# Revit family: RN 81035 Optipress-Aquaplus-Übergang
name_source: partatom
category: Rohrformteile
units: mm (PartAtom-declared; Revit-internal decimal feet)

## family parameters
Arbeitsebenenbasiert = Nein
Beim Laden mit Abzugskörper schneiden = Nein
Bemaßung runder Anschluss = Durchmesser verwenden
Gemeinsam genutzt = Nein
Immer vertikal = Ja
Teiletyp = Verbindung

## types (20) — shared parameters
1.010.00.2 Blattnummer der Richtlinie = 29
1.010.00.3 Ausgabedatum (Monat) der Richtlinie = 201308
1.010.00.4 Herstellername = R. Nussbaum AG
1.010.00.5 Revisionsdatum der Datei = 20190521
1.010.00.6 Webadresse des Herstellers = http://www.nussbaum.ch
1.100.00.4 Produktbezeichnung = Versorgung
1.110.00.2 Index = 4
1.110.00.4 Produktbezeichnung = Optipress
1.960/3L.00.8 Link (URL) = https://www.nussbaum.ch
29.700.00.4 Produktname = Optipress-Aquaplus-Übergang, mit Aussengewinde
29.700.00.5 Produktkennung = 2
29.700.00.6 Querschnittsform = 1
29.700.00.7 Nennweitensystem = DN
29.700.00.8 Nenndrucksystem = PN
29.710.02.4 Nenndruck = 16
29.710.02.5 max. zul. Überdruck [hPa] = 1600
29.710.02.7 max. zul. Dauer-Betriebsdruck [hPa] = 1600
29.710.02.9 max. zul. Dauer-Betriebstemperatur [°C] = 95
Connector Visibility = Nein
EnclosingSpace Visibility = Nein

## per-type parameters (varying)
- 81035.18, Optipress-Aquaplus-Übergang, mit Aussengewinde, DN=10, L=35, R=3/8: 1.800.00.3 TGA-Nummer=01900400000000000000000000000000000000000000000024000000000000000020; 1.810.00.3 Hersteller-Bestellnummer=81035.18; 1.810.00.4 DATANORM-Nummer=81035.18; 1.810.00.6 GTIN-Nummer=7612945021618; 29.710.02.10 Formstück-Gewicht [kg]=0.03; 29.710.02.3 Benennung=Optipress-Aquaplus-Übergang, mit Aussengewinde, DN=10, L=35, R=3/8; CONNECTOR0_DIAMETER_dX_0r=10 mm  [stored 0.0328084 ft]; CONNECTOR0_dX_01=18 mm; CONNECTOR0_ref_dX=18 mm; CONNECTOR1_DIAMETER_dX_0r=12 mm  [stored 0.0393701 ft]; CONNECTOR1_dX_00=25 mm  [stored 0.082021 ft]; CONNECTOR1_dX_01=35 mm; CONNECTOR1_ref_dX=25 mm  [stored 0.082021 ft]; R. Nussbaum AG 81035.18 de Visibility=Ja; R. Nussbaum AG 81035.19 de Visibility=Nein; R. Nussbaum AG 81035.20 de Visibility=Nein; R. Nussbaum AG 81035.21 de Visibility=Nein; R. Nussbaum AG 81035.22 de Visibility=Nein; R. Nussbaum AG 81035.23 de Visibility=Nein; R. Nussbaum AG 81035.24 de Visibility=Nein; R. Nussbaum AG 81035.25 de Visibility=Nein; R. Nussbaum AG 81035.27 de Visibility=Nein; R. Nussbaum AG 81035.28 de Visibility=Nein; R. Nussbaum AG 81035.29 de Visibility=Nein; R. Nussbaum AG 81035.30 de Visibility=Nein; R. Nussbaum AG 81035.31 de Visibility=Nein; R. Nussbaum AG 81035.32 de Visibility=Nein; R. Nussbaum AG 81035.33 de Visibility=Nein; R. Nussbaum AG 81035.34 de Visibility=Nein; R. Nussbaum AG 81035.36 de Visibility=Nein; R. Nussbaum AG 81035.37 de Visibility=Nein; R. Nussbaum AG 81035.38 de Visibility=Nein; R. Nussbaum AG 81035.39 de Visibility=Nein
- 81035.19, Optipress-Aquaplus-Übergang, mit Aussengewinde, DN=10x15, L=37, R=½: 1.800.00.3 TGA-Nummer=01900400000000000000000000000000000000000000000024000000000000000021; 1.810.00.3 Hersteller-Bestellnummer=81035.19; 1.810.00.4 DATANORM-Nummer=81035.19; 1.810.00.5 StLB-Nummer=267.111; 1.810.00.6 GTIN-Nummer=7612945021625; 29.710.02.10 Formstück-Gewicht [kg]=0.036; 29.710.02.3 Benennung=Optipress-Aquaplus-Übergang, mit Aussengewinde, DN=10x15, L=37, R=½; CONNECTOR0_DIAMETER_dX_0r=12 mm  [stored 0.0393701 ft]; CONNECTOR0_dX_01=18 mm; CONNECTOR0_ref_dX=18 mm; CONNECTOR1_DIAMETER_dX_0r=15 mm  [stored 0.0492126 ft]; CONNECTOR1_dX_00=24 mm  [stored 0.0787402 ft]; CONNECTOR1_dX_01=37 mm; CONNECTOR1_ref_dX=24 mm  [stored 0.0787402 ft]; R. Nussbaum AG 81035.18 de Visibility=Nein; R. Nussbaum AG 81035.19 de Visibility=Ja; R. Nussbaum AG 81035.20 de Visibility=Nein; R. Nussbaum AG 81035.21 de Visibility=Nein; R. Nussbaum AG 81035.22 de Visibility=Nein; R. Nussbaum AG 81035.23 de Visibility=Nein; R. Nussbaum AG 81035.24 de Visibility=Nein; R. Nussbaum AG 81035.25 de Visibility=Nein; R. Nussbaum AG 81035.27 de Visibility=Nein; R. Nussbaum AG 81035.28 de Visibility=Nein; R. Nussbaum AG 81035.29 de Visibility=Nein; R. Nussbaum AG 81035.30 de Visibility=Nein; R. Nussbaum AG 81035.31 de Visibility=Nein; R. Nussbaum AG 81035.32 de Visibility=Nein; R. Nussbaum AG 81035.33 de Visibility=Nein; R. Nussbaum AG 81035.34 de Visibility=Nein; R. Nussbaum AG 81035.36 de Visibility=Nein; R. Nussbaum AG 81035.37 de Visibility=Nein; R. Nussbaum AG 81035.38 de Visibility=Nein; R. Nussbaum AG 81035.39 de Visibility=Nein
- 81035.21, Optipress-Aquaplus-Übergang, mit Aussengewinde, DN=12x15, L=46, R=½: 1.800.00.3 TGA-Nummer=01900400000000000000000000000000000000000000000024000000000000000022; 1.810.00.3 Hersteller-Bestellnummer=81035.21; 1.810.00.4 DATANORM-Nummer=81035.21; 1.810.00.5 StLB-Nummer=267.112; 1.810.00.6 GTIN-Nummer=7612945021649; 29.710.02.10 Formstück-Gewicht [kg]=0.046; 29.710.02.3 Benennung=Optipress-Aquaplus-Übergang, mit Aussengewinde, DN=12x15, L=46, R=½; CONNECTOR0_DIAMETER_dX_0r=12 mm  [stored 0.0393701 ft]; CONNECTOR0_dX_01=22 mm; CONNECTOR0_ref_dX=22 mm; CONNECTOR1_DIAMETER_dX_0r=15 mm  [stored 0.0492126 ft]; CONNECTOR1_dX_00=33 mm; CONNECTOR1_dX_01=46 mm; CONNECTOR1_ref_dX=33 mm; R. Nussbaum AG 81035.18 de Visibility=Nein; R. Nussbaum AG 81035.19 de Visibility=Nein; R. Nussbaum AG 81035.20 de Visibility=Nein; R. Nussbaum AG 81035.21 de Visibility=Ja; R. Nussbaum AG 81035.22 de Visibility=Nein; R. Nussbaum AG 81035.23 de Visibility=Nein; R. Nussbaum AG 81035.24 de Visibility=Nein; R. Nussbaum AG 81035.25 de Visibility=Nein; R. Nussbaum AG 81035.27 de Visibility=Nein; R. Nussbaum AG 81035.28 de Visibility=Nein; R. Nussbaum AG 81035.29 de Visibility=Nein; R. Nussbaum AG 81035.30 de Visibility=Nein; R. Nussbaum AG 81035.31 de Visibility=Nein; R. Nussbaum AG 81035.32 de Visibility=Nein; R. Nussbaum AG 81035.33 de Visibility=Nein; R. Nussbaum AG 81035.34 de Visibility=Nein; R. Nussbaum AG 81035.36 de Visibility=Nein; R. Nussbaum AG 81035.37 de Visibility=Nein; R. Nussbaum AG 81035.38 de Visibility=Nein; R. Nussbaum AG 81035.39 de Visibility=Nein
- 81035.22, Optipress-Aquaplus-Übergang, mit Aussengewinde, DN=15x20, L=50, R=¾: 1.800.00.3 TGA-Nummer=01900400000000000000000000000000000000000000000024000000000000000023; 1.810.00.3 Hersteller-Bestellnummer=81035.22; 1.810.00.4 DATANORM-Nummer=81035.22; 1.810.00.6 GTIN-Nummer=7612945021656; 29.710.02.10 Formstück-Gewicht [kg]=0.065; 29.710.02.3 Benennung=Optipress-Aquaplus-Übergang, mit Aussengewinde, DN=15x20, L=50, R=¾; CONNECTOR0_DIAMETER_dX_0r=15 mm  [stored 0.0492126 ft]; CONNECTOR0_dX_01=22 mm; CONNECTOR0_ref_dX=22 mm; CONNECTOR1_DIAMETER_dX_0r=20 mm; CONNECTOR1_dX_00=35 mm; CONNECTOR1_dX_01=50 mm; CONNECTOR1_ref_dX=35 mm; R. Nussbaum AG 81035.18 de Visibility=Nein; R. Nussbaum AG 81035.19 de Visibility=Nein; R. Nussbaum AG 81035.20 de Visibility=Nein; R. Nussbaum AG 81035.21 de Visibility=Nein; R. Nussbaum AG 81035.22 de Visibility=Ja; R. Nussbaum AG 81035.23 de Visibility=Nein; R. Nussbaum AG 81035.24 de Visibility=Nein; R. Nussbaum AG 81035.25 de Visibility=Nein; R. Nussbaum AG 81035.27 de Visibility=Nein; R. Nussbaum AG 81035.28 de Visibility=Nein; R. Nussbaum AG 81035.29 de Visibility=Nein; R. Nussbaum AG 81035.30 de Visibility=Nein; R. Nussbaum AG 81035.31 de Visibility=Nein; R. Nussbaum AG 81035.32 de Visibility=Nein; R. Nussbaum AG 81035.33 de Visibility=Nein; R. Nussbaum AG 81035.34 de Visibility=Nein; R. Nussbaum AG 81035.36 de Visibility=Nein; R. Nussbaum AG 81035.37 de Visibility=Nein; R. Nussbaum AG 81035.38 de Visibility=Nein; R. Nussbaum AG 81035.39 de Visibility=Nein
- 81035.23, Optipress-Aquaplus-Übergang, mit Aussengewinde, DN=15, L=45, R=½: 1.800.00.3 TGA-Nummer=01900400000000000000000000000000000000000000000024000000000000000024; 1.810.00.3 Hersteller-Bestellnummer=81035.23; 1.810.00.4 DATANORM-Nummer=81035.23; 1.810.00.5 StLB-Nummer=267.113; 1.810.00.6 GTIN-Nummer=7612945021663; 29.710.02.10 Formstück-Gewicht [kg]=0.05; 29.710.02.3 Benennung=Optipress-Aquaplus-Übergang, mit Aussengewinde, DN=15, L=45, R=½; CONNECTOR0_DIAMETER_dX_0r=15 mm  [stored 0.0492126 ft]; CONNECTOR0_dX_01=22 mm; CONNECTOR0_ref_dX=22 mm; CONNECTOR1_DIAMETER_dX_0r=15 mm  [stored 0.0492126 ft]; CONNECTOR1_dX_00=32 mm; CONNECTOR1_dX_01=45 mm; CONNECTOR1_ref_dX=32 mm; R. Nussbaum AG 81035.18 de Visibility=Nein; R. Nussbaum AG 81035.19 de Visibility=Nein; R. Nussbaum AG 81035.20 de Visibility=Nein; R. Nussbaum AG 81035.21 de Visibility=Nein; R. Nussbaum AG 81035.22 de Visibility=Nein; R. Nussbaum AG 81035.23 de Visibility=Ja; R. Nussbaum AG 81035.24 de Visibility=Nein; R. Nussbaum AG 81035.25 de Visibility=Nein; R. Nussbaum AG 81035.27 de Visibility=Nein; R. Nussbaum AG 81035.28 de Visibility=Nein; R. Nussbaum AG 81035.29 de Visibility=Nein; R. Nussbaum AG 81035.30 de Visibility=Nein; R. Nussbaum AG 81035.31 de Visibility=Nein; R. Nussbaum AG 81035.32 de Visibility=Nein; R. Nussbaum AG 81035.33 de Visibility=Nein; R. Nussbaum AG 81035.34 de Visibility=Nein; R. Nussbaum AG 81035.36 de Visibility=Nein; R. Nussbaum AG 81035.37 de Visibility=Nein; R. Nussbaum AG 81035.38 de Visibility=Nein; R. Nussbaum AG 81035.39 de Visibility=Nein
- 81035.24, Optipress-Aquaplus-Übergang, mit Aussengewinde, DN=15x20, L=49, R=¾: 1.800.00.3 TGA-Nummer=01900400000000000000000000000000000000000000000024000000000000000025; 1.810.00.3 Hersteller-Bestellnummer=81035.24; 1.810.00.4 DATANORM-Nummer=81035.24; 1.810.00.6 GTIN-Nummer=7612945021670; 29.710.02.10 Formstück-Gewicht [kg]=0.07; 29.710.02.3 Benennung=Optipress-Aquaplus-Übergang, mit Aussengewinde, DN=15x20, L=49, R=¾; CONNECTOR0_DIAMETER_dX_0r=15 mm  [stored 0.0492126 ft]; CONNECTOR0_dX_01=22 mm; CONNECTOR0_ref_dX=22 mm; CONNECTOR1_DIAMETER_dX_0r=20 mm; CONNECTOR1_dX_00=34 mm; CONNECTOR1_dX_01=49 mm; CONNECTOR1_ref_dX=34 mm; R. Nussbaum AG 81035.18 de Visibility=Nein; R. Nussbaum AG 81035.19 de Visibility=Nein; R. Nussbaum AG 81035.20 de Visibility=Nein; R. Nussbaum AG 81035.21 de Visibility=Nein; R. Nussbaum AG 81035.22 de Visibility=Nein; R. Nussbaum AG 81035.23 de Visibility=Nein; R. Nussbaum AG 81035.24 de Visibility=Ja; R. Nussbaum AG 81035.25 de Visibility=Nein; R. Nussbaum AG 81035.27 de Visibility=Nein; R. Nussbaum AG 81035.28 de Visibility=Nein; R. Nussbaum AG 81035.29 de Visibility=Nein; R. Nussbaum AG 81035.30 de Visibility=Nein; R. Nussbaum AG 81035.31 de Visibility=Nein; R. Nussbaum AG 81035.32 de Visibility=Nein; R. Nussbaum AG 81035.33 de Visibility=Nein; R. Nussbaum AG 81035.34 de Visibility=Nein; R. Nussbaum AG 81035.36 de Visibility=Nein; R. Nussbaum AG 81035.37 de Visibility=Nein; R. Nussbaum AG 81035.38 de Visibility=Nein; R. Nussbaum AG 81035.39 de Visibility=Nein
- 81035.25, Optipress-Aquaplus-Übergang, mit Aussengewinde, DN=20, L=49, R=¾: 1.800.00.3 TGA-Nummer=01900400000000000000000000000000000000000000000024000000000000000026; 1.810.00.3 Hersteller-Bestellnummer=81035.25; 1.810.00.4 DATANORM-Nummer=81035.25; 1.810.00.5 StLB-Nummer=267.114; 1.810.00.6 GTIN-Nummer=7612945021687; 29.710.02.10 Formstück-Gewicht [kg]=0.076; 29.710.02.3 Benennung=Optipress-Aquaplus-Übergang, mit Aussengewinde, DN=20, L=49, R=¾; CONNECTOR0_DIAMETER_dX_0r=20 mm; CONNECTOR0_dX_01=24 mm  [stored 0.0787402 ft]; CONNECTOR0_ref_dX=24 mm  [stored 0.0787402 ft]; CONNECTOR1_DIAMETER_dX_0r=20 mm; CONNECTOR1_dX_00=34 mm; CONNECTOR1_dX_01=49 mm; CONNECTOR1_ref_dX=34 mm; R. Nussbaum AG 81035.18 de Visibility=Nein; R. Nussbaum AG 81035.19 de Visibility=Nein; R. Nussbaum AG 81035.20 de Visibility=Nein; R. Nussbaum AG 81035.21 de Visibility=Nein; R. Nussbaum AG 81035.22 de Visibility=Nein; R. Nussbaum AG 81035.23 de Visibility=Nein; R. Nussbaum AG 81035.24 de Visibility=Nein; R. Nussbaum AG 81035.25 de Visibility=Ja; R. Nussbaum AG 81035.27 de Visibility=Nein; R. Nussbaum AG 81035.28 de Visibility=Nein; R. Nussbaum AG 81035.29 de Visibility=Nein; R. Nussbaum AG 81035.30 de Visibility=Nein; R. Nussbaum AG 81035.31 de Visibility=Nein; R. Nussbaum AG 81035.32 de Visibility=Nein; R. Nussbaum AG 81035.33 de Visibility=Nein; R. Nussbaum AG 81035.34 de Visibility=Nein; R. Nussbaum AG 81035.36 de Visibility=Nein; R. Nussbaum AG 81035.37 de Visibility=Nein; R. Nussbaum AG 81035.38 de Visibility=Nein; R. Nussbaum AG 81035.39 de Visibility=Nein
- 81035.27, Optipress-Aquaplus-Übergang, mit Aussengewinde, DN=20x25, L=56, R=1: 1.800.00.3 TGA-Nummer=01900400000000000000000000000000000000000000000024000000000000000027; 1.810.00.3 Hersteller-Bestellnummer=81035.27; 1.810.00.4 DATANORM-Nummer=81035.27; 1.810.00.6 GTIN-Nummer=7612945021694; 29.710.02.10 Formstück-Gewicht [kg]=0.108; 29.710.02.3 Benennung=Optipress-Aquaplus-Übergang, mit Aussengewinde, DN=20x25, L=56, R=1; CONNECTOR0_DIAMETER_dX_0r=20 mm; CONNECTOR0_dX_01=24 mm  [stored 0.0787402 ft]; CONNECTOR0_ref_dX=24 mm  [stored 0.0787402 ft]; CONNECTOR1_DIAMETER_dX_0r=25 mm  [stored 0.082021 ft]; CONNECTOR1_dX_00=39 mm; CONNECTOR1_dX_01=56 mm; CONNECTOR1_ref_dX=39 mm; R. Nussbaum AG 81035.18 de Visibility=Nein; R. Nussbaum AG 81035.19 de Visibility=Nein; R. Nussbaum AG 81035.20 de Visibility=Nein; R. Nussbaum AG 81035.21 de Visibility=Nein; R. Nussbaum AG 81035.22 de Visibility=Nein; R. Nussbaum AG 81035.23 de Visibility=Nein; R. Nussbaum AG 81035.24 de Visibility=Nein; R. Nussbaum AG 81035.25 de Visibility=Nein; R. Nussbaum AG 81035.27 de Visibility=Ja; R. Nussbaum AG 81035.28 de Visibility=Nein; R. Nussbaum AG 81035.29 de Visibility=Nein; R. Nussbaum AG 81035.30 de Visibility=Nein; R. Nussbaum AG 81035.31 de Visibility=Nein; R. Nussbaum AG 81035.32 de Visibility=Nein; R. Nussbaum AG 81035.33 de Visibility=Nein; R. Nussbaum AG 81035.34 de Visibility=Nein; R. Nussbaum AG 81035.36 de Visibility=Nein; R. Nussbaum AG 81035.37 de Visibility=Nein; R. Nussbaum AG 81035.38 de Visibility=Nein; R. Nussbaum AG 81035.39 de Visibility=Nein
- 81035.28, Optipress-Aquaplus-Übergang, mit Aussengewinde, DN=25x20, L=52, R=¾: 1.800.00.3 TGA-Nummer=01900400000000000000000000000000000000000000000024000000000000000028; 1.810.00.3 Hersteller-Bestellnummer=81035.28; 1.810.00.4 DATANORM-Nummer=81035.28; 1.810.00.6 GTIN-Nummer=7612945021700; 29.710.02.10 Formstück-Gewicht [kg]=0.098; 29.710.02.3 Benennung=Optipress-Aquaplus-Übergang, mit Aussengewinde, DN=25x20, L=52, R=¾; CONNECTOR0_DIAMETER_dX_0r=25 mm  [stored 0.082021 ft]; CONNECTOR0_dX_01=24 mm  [stored 0.0787402 ft]; CONNECTOR0_ref_dX=24 mm  [stored 0.0787402 ft]; CONNECTOR1_DIAMETER_dX_0r=20 mm; CONNECTOR1_dX_00=37 mm; CONNECTOR1_dX_01=52 mm; CONNECTOR1_ref_dX=37 mm; R. Nussbaum AG 81035.18 de Visibility=Nein; R. Nussbaum AG 81035.19 de Visibility=Nein; R. Nussbaum AG 81035.20 de Visibility=Nein; R. Nussbaum AG 81035.21 de Visibility=Nein; R. Nussbaum AG 81035.22 de Visibility=Nein; R. Nussbaum AG 81035.23 de Visibility=Nein; R. Nussbaum AG 81035.24 de Visibility=Nein; R. Nussbaum AG 81035.25 de Visibility=Nein; R. Nussbaum AG 81035.27 de Visibility=Nein; R. Nussbaum AG 81035.28 de Visibility=Ja; R. Nussbaum AG 81035.29 de Visibility=Nein; R. Nussbaum AG 81035.30 de Visibility=Nein; R. Nussbaum AG 81035.31 de Visibility=Nein; R. Nussbaum AG 81035.32 de Visibility=Nein; R. Nussbaum AG 81035.33 de Visibility=Nein; R. Nussbaum AG 81035.34 de Visibility=Nein; R. Nussbaum AG 81035.36 de Visibility=Nein; R. Nussbaum AG 81035.37 de Visibility=Nein; R. Nussbaum AG 81035.38 de Visibility=Nein; R. Nussbaum AG 81035.39 de Visibility=Nein
- 81035.29, Optipress-Aquaplus-Übergang, mit Aussengewinde, DN=25, L=55, R=1: 1.800.00.3 TGA-Nummer=01900400000000000000000000000000000000000000000024000000000000000029; 1.810.00.3 Hersteller-Bestellnummer=81035.29; 1.810.00.4 DATANORM-Nummer=81035.29; 1.810.00.5 StLB-Nummer=267.115; 1.810.00.6 GTIN-Nummer=7612945021717; 29.710.02.10 Formstück-Gewicht [kg]=0.114; 29.710.02.3 Benennung=Optipress-Aquaplus-Übergang, mit Aussengewinde, DN=25, L=55, R=1; CONNECTOR0_DIAMETER_dX_0r=25 mm  [stored 0.082021 ft]; CONNECTOR0_dX_01=24 mm  [stored 0.0787402 ft]; CONNECTOR0_ref_dX=24 mm  [stored 0.0787402 ft]; CONNECTOR1_DIAMETER_dX_0r=25 mm  [stored 0.082021 ft]; CONNECTOR1_dX_00=38 mm; CONNECTOR1_dX_01=55 mm  [stored 0.180446 ft]; CONNECTOR1_ref_dX=38 mm; R. Nussbaum AG 81035.18 de Visibility=Nein; R. Nussbaum AG 81035.19 de Visibility=Nein; R. Nussbaum AG 81035.20 de Visibility=Nein; R. Nussbaum AG 81035.21 de Visibility=Nein; R. Nussbaum AG 81035.22 de Visibility=Nein; R. Nussbaum AG 81035.23 de Visibility=Nein; R. Nussbaum AG 81035.24 de Visibility=Nein; R. Nussbaum AG 81035.25 de Visibility=Nein; R. Nussbaum AG 81035.27 de Visibility=Nein; R. Nussbaum AG 81035.28 de Visibility=Nein; R. Nussbaum AG 81035.29 de Visibility=Ja; R. Nussbaum AG 81035.30 de Visibility=Nein; R. Nussbaum AG 81035.31 de Visibility=Nein; R. Nussbaum AG 81035.32 de Visibility=Nein; R. Nussbaum AG 81035.33 de Visibility=Nein; R. Nussbaum AG 81035.34 de Visibility=Nein; R. Nussbaum AG 81035.36 de Visibility=Nein; R. Nussbaum AG 81035.37 de Visibility=Nein; R. Nussbaum AG 81035.38 de Visibility=Nein; R. Nussbaum AG 81035.39 de Visibility=Nein
- 81035.31, Optipress-Aquaplus-Übergang, mit Aussengewinde, DN=32, L=60, R=1¼: 1.800.00.3 TGA-Nummer=01900400000000000000000000000000000000000000000024000000000000000030; 1.810.00.3 Hersteller-Bestellnummer=81035.31; 1.810.00.4 DATANORM-Nummer=81035.31; 1.810.00.5 StLB-Nummer=267.116; 1.810.00.6 GTIN-Nummer=7612945021731; 29.710.02.10 Formstück-Gewicht [kg]=0.185; 29.710.02.3 Benennung=Optipress-Aquaplus-Übergang, mit Aussengewinde, DN=32, L=60, R=1¼; CONNECTOR0_DIAMETER_dX_0r=32 mm; CONNECTOR0_dX_01=26 mm; CONNECTOR0_ref_dX=26 mm; CONNECTOR1_DIAMETER_dX_0r=32 mm; CONNECTOR1_dX_00=41 mm; CONNECTOR1_dX_01=60 mm; CONNECTOR1_ref_dX=41 mm; R. Nussbaum AG 81035.18 de Visibility=Nein; R. Nussbaum AG 81035.19 de Visibility=Nein; R. Nussbaum AG 81035.20 de Visibility=Nein; R. Nussbaum AG 81035.21 de Visibility=Nein; R. Nussbaum AG 81035.22 de Visibility=Nein; R. Nussbaum AG 81035.23 de Visibility=Nein; R. Nussbaum AG 81035.24 de Visibility=Nein; R. Nussbaum AG 81035.25 de Visibility=Nein; R. Nussbaum AG 81035.27 de Visibility=Nein; R. Nussbaum AG 81035.28 de Visibility=Nein; R. Nussbaum AG 81035.29 de Visibility=Nein; R. Nussbaum AG 81035.30 de Visibility=Nein; R. Nussbaum AG 81035.31 de Visibility=Ja; R. Nussbaum AG 81035.32 de Visibility=Nein; R. Nussbaum AG 81035.33 de Visibility=Nein; R. Nussbaum AG 81035.34 de Visibility=Nein; R. Nussbaum AG 81035.36 de Visibility=Nein; R. Nussbaum AG 81035.37 de Visibility=Nein; R. Nussbaum AG 81035.38 de Visibility=Nein; R. Nussbaum AG 81035.39 de Visibility=Nein
- 81035.32, Optipress-Aquaplus-Übergang, mit Aussengewinde, DN=40x32, L=65, R=1¼: 1.800.00.3 TGA-Nummer=01900400000000000000000000000000000000000000000024000000000000000031; 1.810.00.3 Hersteller-Bestellnummer=81035.32; 1.810.00.4 DATANORM-Nummer=81035.32; 1.810.00.6 GTIN-Nummer=7612945021748; 29.710.02.10 Formstück-Gewicht [kg]=0.231; 29.710.02.3 Benennung=Optipress-Aquaplus-Übergang, mit Aussengewinde, DN=40x32, L=65, R=1¼; CONNECTOR0_DIAMETER_dX_0r=40 mm; CONNECTOR0_dX_01=36 mm; CONNECTOR0_ref_dX=36 mm; CONNECTOR1_DIAMETER_dX_0r=32 mm; CONNECTOR1_dX_00=46 mm; CONNECTOR1_dX_01=65 mm; CONNECTOR1_ref_dX=46 mm; R. Nussbaum AG 81035.18 de Visibility=Nein; R. Nussbaum AG 81035.19 de Visibility=Nein; R. Nussbaum AG 81035.20 de Visibility=Nein; R. Nussbaum AG 81035.21 de Visibility=Nein; R. Nussbaum AG 81035.22 de Visibility=Nein; R. Nussbaum AG 81035.23 de Visibility=Nein; R. Nussbaum AG 81035.24 de Visibility=Nein; R. Nussbaum AG 81035.25 de Visibility=Nein; R. Nussbaum AG 81035.27 de Visibility=Nein; R. Nussbaum AG 81035.28 de Visibility=Nein; R. Nussbaum AG 81035.29 de Visibility=Nein; R. Nussbaum AG 81035.30 de Visibility=Nein; R. Nussbaum AG 81035.31 de Visibility=Nein; R. Nussbaum AG 81035.32 de Visibility=Ja; R. Nussbaum AG 81035.33 de Visibility=Nein; R. Nussbaum AG 81035.34 de Visibility=Nein; R. Nussbaum AG 81035.36 de Visibility=Nein; R. Nussbaum AG 81035.37 de Visibility=Nein; R. Nussbaum AG 81035.38 de Visibility=Nein; R. Nussbaum AG 81035.39 de Visibility=Nein
- 81035.33, Optipress-Aquaplus-Übergang, mit Aussengewinde, DN=40, L=66, R=1½: 1.800.00.3 TGA-Nummer=01900400000000000000000000000000000000000000000024000000000000000032; 1.810.00.3 Hersteller-Bestellnummer=81035.33; 1.810.00.4 DATANORM-Nummer=81035.33; 1.810.00.5 StLB-Nummer=267.117; 1.810.00.6 GTIN-Nummer=7612945021755; 29.710.02.10 Formstück-Gewicht [kg]=0.255; 29.710.02.3 Benennung=Optipress-Aquaplus-Übergang, mit Aussengewinde, DN=40, L=66, R=1½; CONNECTOR0_DIAMETER_dX_0r=40 mm; CONNECTOR0_dX_01=36 mm; CONNECTOR0_ref_dX=36 mm; CONNECTOR1_DIAMETER_dX_0r=40 mm; CONNECTOR1_dX_00=47 mm; CONNECTOR1_dX_01=66 mm; CONNECTOR1_ref_dX=47 mm; R. Nussbaum AG 81035.18 de Visibility=Nein; R. Nussbaum AG 81035.19 de Visibility=Nein; R. Nussbaum AG 81035.20 de Visibility=Nein; R. Nussbaum AG 81035.21 de Visibility=Nein; R. Nussbaum AG 81035.22 de Visibility=Nein; R. Nussbaum AG 81035.23 de Visibility=Nein; R. Nussbaum AG 81035.24 de Visibility=Nein; R. Nussbaum AG 81035.25 de Visibility=Nein; R. Nussbaum AG 81035.27 de Visibility=Nein; R. Nussbaum AG 81035.28 de Visibility=Nein; R. Nussbaum AG 81035.29 de Visibility=Nein; R. Nussbaum AG 81035.30 de Visibility=Nein; R. Nussbaum AG 81035.31 de Visibility=Nein; R. Nussbaum AG 81035.32 de Visibility=Nein; R. Nussbaum AG 81035.33 de Visibility=Ja; R. Nussbaum AG 81035.34 de Visibility=Nein; R. Nussbaum AG 81035.36 de Visibility=Nein; R. Nussbaum AG 81035.37 de Visibility=Nein; R. Nussbaum AG 81035.38 de Visibility=Nein; R. Nussbaum AG 81035.39 de Visibility=Nein
- 81035.34, Optipress-Aquaplus-Übergang, mit Aussengewinde, DN=50, L=80, R=2: 1.800.00.3 TGA-Nummer=01900400000000000000000000000000000000000000000024000000000000000033; 1.810.00.3 Hersteller-Bestellnummer=81035.34; 1.810.00.4 DATANORM-Nummer=81035.34; 1.810.00.5 StLB-Nummer=267.118; 1.810.00.6 GTIN-Nummer=7612945021762; 29.710.02.10 Formstück-Gewicht [kg]=0.508; 29.710.02.3 Benennung=Optipress-Aquaplus-Übergang, mit Aussengewinde, DN=50, L=80, R=2; CONNECTOR0_DIAMETER_dX_0r=50 mm; CONNECTOR0_dX_01=40 mm; CONNECTOR0_ref_dX=40 mm; CONNECTOR1_DIAMETER_dX_0r=50 mm; CONNECTOR1_dX_00=55 mm  [stored 0.180446 ft]; CONNECTOR1_dX_01=79 mm; CONNECTOR1_ref_dX=55 mm  [stored 0.180446 ft]; R. Nussbaum AG 81035.18 de Visibility=Nein; R. Nussbaum AG 81035.19 de Visibility=Nein; R. Nussbaum AG 81035.20 de Visibility=Nein; R. Nussbaum AG 81035.21 de Visibility=Nein; R. Nussbaum AG 81035.22 de Visibility=Nein; R. Nussbaum AG 81035.23 de Visibility=Nein; R. Nussbaum AG 81035.24 de Visibility=Nein; R. Nussbaum AG 81035.25 de Visibility=Nein; R. Nussbaum AG 81035.27 de Visibility=Nein; R. Nussbaum AG 81035.28 de Visibility=Nein; R. Nussbaum AG 81035.29 de Visibility=Nein; R. Nussbaum AG 81035.30 de Visibility=Nein; R. Nussbaum AG 81035.31 de Visibility=Nein; R. Nussbaum AG 81035.32 de Visibility=Nein; R. Nussbaum AG 81035.33 de Visibility=Nein; R. Nussbaum AG 81035.34 de Visibility=Ja; R. Nussbaum AG 81035.36 de Visibility=Nein; R. Nussbaum AG 81035.37 de Visibility=Nein; R. Nussbaum AG 81035.38 de Visibility=Nein; R. Nussbaum AG 81035.39 de Visibility=Nein
- 81035.36, Optipress-Aquaplus-Übergang, mit Aussengewinde, DN=20x15, L=49, R=½: 1.800.00.3 TGA-Nummer=01900400000000000000000000000000000000000000000024000000000000000034; 1.810.00.3 Hersteller-Bestellnummer=81035.36; 1.810.00.4 DATANORM-Nummer=81035.36; 1.810.00.6 GTIN-Nummer=7612945021779; 29.710.02.10 Formstück-Gewicht [kg]=0.07; 29.710.02.3 Benennung=Optipress-Aquaplus-Übergang, mit Aussengewinde, DN=20x15, L=49, R=½; CONNECTOR0_DIAMETER_dX_0r=20 mm; CONNECTOR0_dX_01=24 mm  [stored 0.0787402 ft]; CONNECTOR0_ref_dX=24 mm  [stored 0.0787402 ft]; CONNECTOR1_DIAMETER_dX_0r=15 mm  [stored 0.0492126 ft]; CONNECTOR1_dX_00=36 mm; CONNECTOR1_dX_01=49 mm; CONNECTOR1_ref_dX=36 mm; R. Nussbaum AG 81035.18 de Visibility=Nein; R. Nussbaum AG 81035.19 de Visibility=Nein; R. Nussbaum AG 81035.20 de Visibility=Nein; R. Nussbaum AG 81035.21 de Visibility=Nein; R. Nussbaum AG 81035.22 de Visibility=Nein; R. Nussbaum AG 81035.23 de Visibility=Nein; R. Nussbaum AG 81035.24 de Visibility=Nein; R. Nussbaum AG 81035.25 de Visibility=Nein; R. Nussbaum AG 81035.27 de Visibility=Nein; R. Nussbaum AG 81035.28 de Visibility=Nein; R. Nussbaum AG 81035.29 de Visibility=Nein; R. Nussbaum AG 81035.30 de Visibility=Nein; R. Nussbaum AG 81035.31 de Visibility=Nein; R. Nussbaum AG 81035.32 de Visibility=Nein; R. Nussbaum AG 81035.33 de Visibility=Nein; R. Nussbaum AG 81035.34 de Visibility=Nein; R. Nussbaum AG 81035.36 de Visibility=Ja; R. Nussbaum AG 81035.37 de Visibility=Nein; R. Nussbaum AG 81035.38 de Visibility=Nein; R. Nussbaum AG 81035.39 de Visibility=Nein
- 81035.37, Optipress-Aquaplus-Übergang, mit Aussengewinde, DN=32x25, L=56, R=1: 1.800.00.3 TGA-Nummer=01900400000000000000000000000000000000000000000024000000000000000035; 1.810.00.3 Hersteller-Bestellnummer=81035.37; 1.810.00.4 DATANORM-Nummer=81035.37; 1.810.00.6 GTIN-Nummer=7612945021786; 29.710.02.10 Formstück-Gewicht [kg]=0.132; 29.710.02.3 Benennung=Optipress-Aquaplus-Übergang, mit Aussengewinde, DN=32x25, L=56, R=1; CONNECTOR0_DIAMETER_dX_0r=32 mm; CONNECTOR0_dX_01=26 mm; CONNECTOR0_ref_dX=26 mm; CONNECTOR1_DIAMETER_dX_0r=25 mm  [stored 0.082021 ft]; CONNECTOR1_dX_00=39 mm; CONNECTOR1_dX_01=56 mm; CONNECTOR1_ref_dX=39 mm; R. Nussbaum AG 81035.18 de Visibility=Nein; R. Nussbaum AG 81035.19 de Visibility=Nein; R. Nussbaum AG 81035.20 de Visibility=Nein; R. Nussbaum AG 81035.21 de Visibility=Nein; R. Nussbaum AG 81035.22 de Visibility=Nein; R. Nussbaum AG 81035.23 de Visibility=Nein; R. Nussbaum AG 81035.24 de Visibility=Nein; R. Nussbaum AG 81035.25 de Visibility=Nein; R. Nussbaum AG 81035.27 de Visibility=Nein; R. Nussbaum AG 81035.28 de Visibility=Nein; R. Nussbaum AG 81035.29 de Visibility=Nein; R. Nussbaum AG 81035.30 de Visibility=Nein; R. Nussbaum AG 81035.31 de Visibility=Nein; R. Nussbaum AG 81035.32 de Visibility=Nein; R. Nussbaum AG 81035.33 de Visibility=Nein; R. Nussbaum AG 81035.34 de Visibility=Nein; R. Nussbaum AG 81035.36 de Visibility=Nein; R. Nussbaum AG 81035.37 de Visibility=Ja; R. Nussbaum AG 81035.38 de Visibility=Nein; R. Nussbaum AG 81035.39 de Visibility=Nein
- 81035.38, Optipress-Aquaplus-Übergang, mit Aussengewinde, DN=32, L=62, R=1½: 1.800.00.3 TGA-Nummer=01900400000000000000000000000000000000000000000024000000000000000036; 1.810.00.3 Hersteller-Bestellnummer=81035.38; 1.810.00.4 DATANORM-Nummer=81035.38; 1.810.00.6 GTIN-Nummer=7612945021793; 29.710.02.10 Formstück-Gewicht [kg]=0.227; 29.710.02.3 Benennung=Optipress-Aquaplus-Übergang, mit Aussengewinde, DN=32, L=62, R=1½; CONNECTOR0_DIAMETER_dX_0r=32 mm; CONNECTOR0_dX_01=26 mm; CONNECTOR0_ref_dX=26 mm; CONNECTOR1_DIAMETER_dX_0r=40 mm; CONNECTOR1_dX_00=43 mm; CONNECTOR1_dX_01=62 mm; CONNECTOR1_ref_dX=43 mm; R. Nussbaum AG 81035.18 de Visibility=Nein; R. Nussbaum AG 81035.19 de Visibility=Nein; R. Nussbaum AG 81035.20 de Visibility=Nein; R. Nussbaum AG 81035.21 de Visibility=Nein; R. Nussbaum AG 81035.22 de Visibility=Nein; R. Nussbaum AG 81035.23 de Visibility=Nein; R. Nussbaum AG 81035.24 de Visibility=Nein; R. Nussbaum AG 81035.25 de Visibility=Nein; R. Nussbaum AG 81035.27 de Visibility=Nein; R. Nussbaum AG 81035.28 de Visibility=Nein; R. Nussbaum AG 81035.29 de Visibility=Nein; R. Nussbaum AG 81035.30 de Visibility=Nein; R. Nussbaum AG 81035.31 de Visibility=Nein; R. Nussbaum AG 81035.32 de Visibility=Nein; R. Nussbaum AG 81035.33 de Visibility=Nein; R. Nussbaum AG 81035.34 de Visibility=Nein; R. Nussbaum AG 81035.36 de Visibility=Nein; R. Nussbaum AG 81035.37 de Visibility=Nein; R. Nussbaum AG 81035.38 de Visibility=Ja; R. Nussbaum AG 81035.39 de Visibility=Nein
- 81035.39, Optipress-Aquaplus-Übergang, mit Aussengewinde, DN=50x40, L=78, R=1½: 1.800.00.3 TGA-Nummer=01900400000000000000000000000000000000000000000024000000000000000037; 1.810.00.3 Hersteller-Bestellnummer=81035.39; 1.810.00.4 DATANORM-Nummer=81035.39; 1.810.00.6 GTIN-Nummer=7612945021809; 29.710.02.10 Formstück-Gewicht [kg]=0.486; 29.710.02.3 Benennung=Optipress-Aquaplus-Übergang, mit Aussengewinde, DN=50x40, L=78, R=1½; CONNECTOR0_DIAMETER_dX_0r=50 mm; CONNECTOR0_dX_01=40 mm; CONNECTOR0_ref_dX=40 mm; CONNECTOR1_DIAMETER_dX_0r=40 mm; CONNECTOR1_dX_00=59 mm; CONNECTOR1_dX_01=78 mm; CONNECTOR1_ref_dX=59 mm; R. Nussbaum AG 81035.18 de Visibility=Nein; R. Nussbaum AG 81035.19 de Visibility=Nein; R. Nussbaum AG 81035.20 de Visibility=Nein; R. Nussbaum AG 81035.21 de Visibility=Nein; R. Nussbaum AG 81035.22 de Visibility=Nein; R. Nussbaum AG 81035.23 de Visibility=Nein; R. Nussbaum AG 81035.24 de Visibility=Nein; R. Nussbaum AG 81035.25 de Visibility=Nein; R. Nussbaum AG 81035.27 de Visibility=Nein; R. Nussbaum AG 81035.28 de Visibility=Nein; R. Nussbaum AG 81035.29 de Visibility=Nein; R. Nussbaum AG 81035.30 de Visibility=Nein; R. Nussbaum AG 81035.31 de Visibility=Nein; R. Nussbaum AG 81035.32 de Visibility=Nein; R. Nussbaum AG 81035.33 de Visibility=Nein; R. Nussbaum AG 81035.34 de Visibility=Nein; R. Nussbaum AG 81035.36 de Visibility=Nein; R. Nussbaum AG 81035.37 de Visibility=Nein; R. Nussbaum AG 81035.38 de Visibility=Nein; R. Nussbaum AG 81035.39 de Visibility=Ja
- 81035.20, Optipress-Aquaplus-Übergang, mit Aussengewinde, DN=15x10, L=42, R=3/8: 1.800.00.3 TGA-Nummer=01900400000000000000000000000000000000000000000024000000000000000040; 1.810.00.3 Hersteller-Bestellnummer=81035.20; 1.810.00.4 DATANORM-Nummer=81035.20; 1.810.00.6 GTIN-Nummer=7612945021632; 29.710.02.10 Formstück-Gewicht [kg]=0.036; 29.710.02.3 Benennung=Optipress-Aquaplus-Übergang, mit Aussengewinde, DN=15x10, L=42, R=3/8; CONNECTOR0_DIAMETER_dX_0r=15 mm  [stored 0.0492126 ft]; CONNECTOR0_dX_01=22 mm; CONNECTOR0_ref_dX=22 mm; CONNECTOR1_DIAMETER_dX_0r=10 mm  [stored 0.0328084 ft]; CONNECTOR1_dX_00=32 mm; CONNECTOR1_dX_01=42 mm; CONNECTOR1_ref_dX=32 mm; R. Nussbaum AG 81035.18 de Visibility=Nein; R. Nussbaum AG 81035.19 de Visibility=Nein; R. Nussbaum AG 81035.20 de Visibility=Ja; R. Nussbaum AG 81035.21 de Visibility=Nein; R. Nussbaum AG 81035.22 de Visibility=Nein; R. Nussbaum AG 81035.23 de Visibility=Nein; R. Nussbaum AG 81035.24 de Visibility=Nein; R. Nussbaum AG 81035.25 de Visibility=Nein; R. Nussbaum AG 81035.27 de Visibility=Nein; R. Nussbaum AG 81035.28 de Visibility=Nein; R. Nussbaum AG 81035.29 de Visibility=Nein; R. Nussbaum AG 81035.30 de Visibility=Nein; R. Nussbaum AG 81035.31 de Visibility=Nein; R. Nussbaum AG 81035.32 de Visibility=Nein; R. Nussbaum AG 81035.33 de Visibility=Nein; R. Nussbaum AG 81035.34 de Visibility=Nein; R. Nussbaum AG 81035.36 de Visibility=Nein; R. Nussbaum AG 81035.37 de Visibility=Nein; R. Nussbaum AG 81035.38 de Visibility=Nein; R. Nussbaum AG 81035.39 de Visibility=Nein
- 81035.30, Optipress-Aquaplus-Übergang, mit Aussengewinde, DN=25x32, L=58, R=1¼: 1.800.00.3 TGA-Nummer=01900400000000000000000000000000000000000000000024000000000000000041; 1.810.00.3 Hersteller-Bestellnummer=81035.30; 1.810.00.4 DATANORM-Nummer=81035.30; 1.810.00.6 GTIN-Nummer=7612945021724; 29.710.02.10 Formstück-Gewicht [kg]=0.156; 29.710.02.3 Benennung=Optipress-Aquaplus-Übergang, mit Aussengewinde, DN=25x32, L=58, R=1¼; CONNECTOR0_DIAMETER_dX_0r=25 mm  [stored 0.082021 ft]; CONNECTOR0_dX_01=24 mm  [stored 0.0787402 ft]; CONNECTOR0_ref_dX=24 mm  [stored 0.0787402 ft]; CONNECTOR1_DIAMETER_dX_0r=32 mm; CONNECTOR1_dX_00=39 mm; CONNECTOR1_dX_01=58 mm; CONNECTOR1_ref_dX=39 mm; R. Nussbaum AG 81035.18 de Visibility=Nein; R. Nussbaum AG 81035.19 de Visibility=Nein; R. Nussbaum AG 81035.20 de Visibility=Nein; R. Nussbaum AG 81035.21 de Visibility=Nein; R. Nussbaum AG 81035.22 de Visibility=Nein; R. Nussbaum AG 81035.23 de Visibility=Nein; R. Nussbaum AG 81035.24 de Visibility=Nein; R. Nussbaum AG 81035.25 de Visibility=Nein; R. Nussbaum AG 81035.27 de Visibility=Nein; R. Nussbaum AG 81035.28 de Visibility=Nein; R. Nussbaum AG 81035.29 de Visibility=Nein; R. Nussbaum AG 81035.30 de Visibility=Ja; R. Nussbaum AG 81035.31 de Visibility=Nein; R. Nussbaum AG 81035.32 de Visibility=Nein; R. Nussbaum AG 81035.33 de Visibility=Nein; R. Nussbaum AG 81035.34 de Visibility=Nein; R. Nussbaum AG 81035.36 de Visibility=Nein; R. Nussbaum AG 81035.37 de Visibility=Nein; R. Nussbaum AG 81035.38 de Visibility=Nein; R. Nussbaum AG 81035.39 de Visibility=Nein

note: column(s) folded — value = type name in every type: 1.800.00.4 Kommentarfeld

note: [stored X ft] marks values corroborated as IEEE doubles in the binary element streams (Revit-internal decimal feet)

## geometry (parser evidence)
native form markers: Sweep x2
no freeform markers — native parametric forms only
